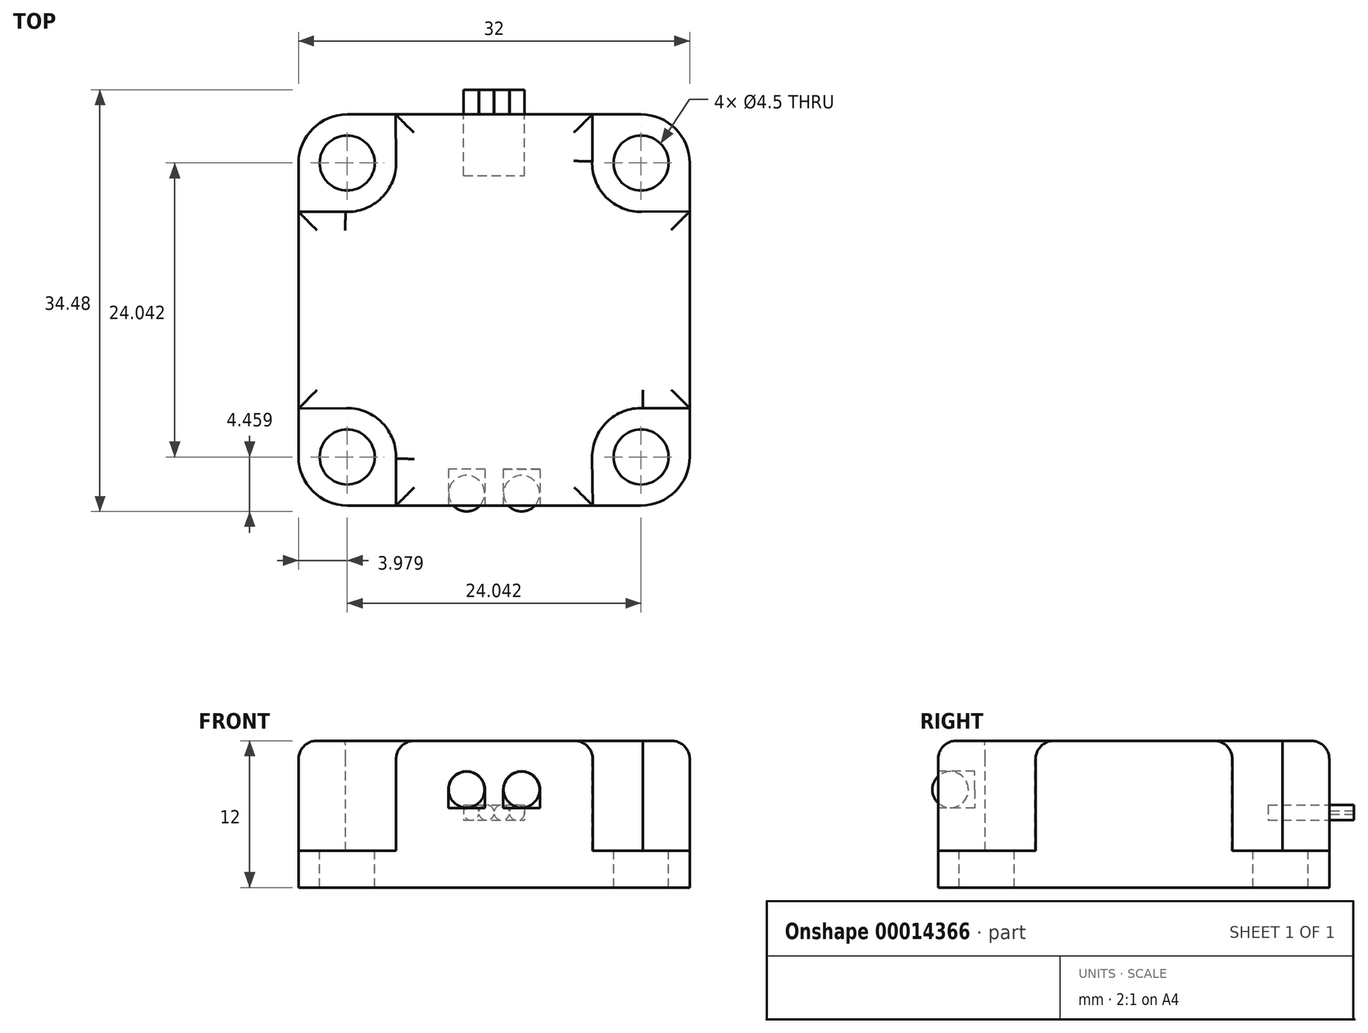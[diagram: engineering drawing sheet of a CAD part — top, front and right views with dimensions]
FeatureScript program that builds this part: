
annotation { "Feature Type Name" : "Feature", "Feature Type Description" : "" }
export const myFeature = defineFeature(function(context is Context, id is Id, definition is map)
    precondition{}
    {
        {
            var Q0;
            Q0=qCreatedBy(makeId("Top.planeOp"),FACE);
            var sketch = newSketch(context, id + "F0", { "sketchPlane" : qUnion([Q0])});
            skLineSegment(sketch, "E0.rect.bottom", {"start": v(16, 16) * mm, "end": v(-16, 16) * mm});
            skLineSegment(sketch, "E0.rect.top", {"start": v(16, -16) * mm, "end": v(-16, -16) * mm});
            skLineSegment(sketch, "E0.rect.left", {"start": v(16, 16) * mm, "end": v(16, -16) * mm});
            skLineSegment(sketch, "E0.rect.right", {"start": v(-16, 16) * mm, "end": v(-16, -16) * mm});
            skPoint(sketch, "E0.rect.middle", {"position": v(0, 0) * mm});
            skSolve(sketch);
        }
        {
            var Q0;
            Q0=qSketchRegion(id+"F0",true);
            extrude(context, id + "F1", {"entities" : qUnion([Q0]), "depth" : 12 * mm});
        }
        {
            var Q0;
            Q0=makeQuery(id+"F1.opExtrude","CAP_FACE",FACE,{"disambiguationData":[OSD([sQuery(id+"F0.wireOp",EDGE,"E0.rect.bottom"),sQuery(id+"F0.wireOp",EDGE,"E0.rect.top"),sQuery(id+"F0.wireOp",EDGE,"E0.rect.left"),sQuery(id+"F0.wireOp",EDGE,"E0.rect.right")])],"isStart":false});
            var sketch = newSketch(context, id + "F2", { "sketchPlane" : qUnion([Q0])});
            skCircle(sketch, "E1", {"center": v(0, 0) * mm, "radius": 17 * mm, "construction": true});
            skLineSegment(sketch, "E2", {"start": v(-16, 16) * mm, "end": v(0, 0) * mm, "construction": true});
            skArc(sketch, "E3", {"start": v(-12.16, 8.02) * mm, "mid": v(-9.22, 9.16) * mm, "end": v(-8.02, 12.07) * mm});
            skLineSegment(sketch, "E4", {"start": v(-8.02, 12.07) * mm, "end": v(-8.07, 16) * mm});
            skLineSegment(sketch, "E5", {"start": v(-8.07, 16) * mm, "end": v(-16, 16) * mm});
            skLineSegment(sketch, "E6", {"start": v(-12.16, 8.02) * mm, "end": v(-16, 8.02) * mm});
            skLineSegment(sketch, "E7", {"start": v(-16, 8.02) * mm, "end": v(-16, 16) * mm});
            skLineSegment(sketch, "E8.1.0", {"start": v(-8.02, -16) * mm, "end": v(-16, -16) * mm});
            skLineSegment(sketch, "E8.1.1", {"start": v(-8.02, -12.16) * mm, "end": v(-8.02, -16) * mm});
            skArc(sketch, "E8.1.2", {"start": v(-8.02, -12.16) * mm, "mid": v(-9.16, -9.22) * mm, "end": v(-12.07, -8.02) * mm});
            skLineSegment(sketch, "E8.1.3", {"start": v(-16, -8.07) * mm, "end": v(-16, -16) * mm});
            skLineSegment(sketch, "E8.1.4", {"start": v(-12.07, -8.02) * mm, "end": v(-16, -8.07) * mm});
            skLineSegment(sketch, "E8.2.0", {"start": v(16, -8.02) * mm, "end": v(16, -16) * mm});
            skLineSegment(sketch, "E8.2.1", {"start": v(12.16, -8.02) * mm, "end": v(16, -8.02) * mm});
            skArc(sketch, "E8.2.2", {"start": v(12.16, -8.02) * mm, "mid": v(9.22, -9.16) * mm, "end": v(8.02, -12.07) * mm});
            skLineSegment(sketch, "E8.2.3", {"start": v(8.07, -16) * mm, "end": v(16, -16) * mm});
            skLineSegment(sketch, "E8.2.4", {"start": v(8.02, -12.07) * mm, "end": v(8.07, -16) * mm});
            skLineSegment(sketch, "E8.3.0", {"start": v(8.02, 16) * mm, "end": v(16, 16) * mm});
            skLineSegment(sketch, "E8.3.1", {"start": v(8.02, 12.16) * mm, "end": v(8.02, 16) * mm});
            skArc(sketch, "E8.3.2", {"start": v(8.02, 12.16) * mm, "mid": v(9.16, 9.22) * mm, "end": v(12.07, 8.02) * mm});
            skLineSegment(sketch, "E8.3.3", {"start": v(16, 8.07) * mm, "end": v(16, 16) * mm});
            skLineSegment(sketch, "E8.3.4", {"start": v(12.07, 8.02) * mm, "end": v(16, 8.07) * mm});
            skSolve(sketch);
        }
        {
            var Q0;
            Q0=qSketchRegion(id+"F2",true);
            extrude(context, id + "F3", {"entities" : qUnion([Q0]), "operationType" : NewBodyOperationType.REMOVE, "oppositeDirection" : true, "depth" : 9 * mm});
        }
        {
            var Q0;
            Q0=makeQuery(id+"F1.opExtrude","SWEPT_EDGE",EDGE,{"disambiguationData":[OSD([sQuery(id+"F0.wireOp",EDGE,"E0.rect.bottom"),sQuery(id+"F0.wireOp",EDGE,"E0.rect.right")])]});
            var Q1;
            Q1=makeQuery(id+"F1.opExtrude","SWEPT_EDGE",EDGE,{"disambiguationData":[OSD([sQuery(id+"F0.wireOp",EDGE,"E0.rect.bottom"),sQuery(id+"F0.wireOp",EDGE,"E0.rect.left")])]});
            var Q2;
            Q2=makeQuery(id+"F1.opExtrude","SWEPT_EDGE",EDGE,{"disambiguationData":[OSD([sQuery(id+"F0.wireOp",EDGE,"E0.rect.top"),sQuery(id+"F0.wireOp",EDGE,"E0.rect.left")])]});
            var Q3;
            Q3=makeQuery(id+"F1.opExtrude","SWEPT_EDGE",EDGE,{"disambiguationData":[OSD([sQuery(id+"F0.wireOp",EDGE,"E0.rect.top"),sQuery(id+"F0.wireOp",EDGE,"E0.rect.right")])]});
            fillet(context, id + "F4", {"entities" : qUnion([Q0, Q1, Q2, Q3]), "radius" : 4 * mm, "tangentPropagation" : true, "allowEdgeOverflow" : false});
        }
        {
            var Q0;
            Q0=makeQuery(id+"F1.opExtrude","CAP_FACE",FACE,{"disambiguationData":[OSD([sQuery(id+"F0.wireOp",EDGE,"E0.rect.bottom"),sQuery(id+"F0.wireOp",EDGE,"E0.rect.top"),sQuery(id+"F0.wireOp",EDGE,"E0.rect.left"),sQuery(id+"F0.wireOp",EDGE,"E0.rect.right")])],"isStart":false});
            var Q1;
            Q1=makeQuery(id+"F3.boolean.opBoolean","COPY",EDGE,{"derivedFrom":makeQuery(id+"F3.opExtrude","SWEPT_EDGE",EDGE,{"disambiguationData":[OSD([sQuery(id+"F0.wireOp",EDGE,"E0.rect.top"),sQuery(id+"F2.wireOp",EDGE,"E8.2.3"),sQuery(id+"F2.wireOp",EDGE,"E8.2.4")])]})});
            var Q2;
            Q2=makeQuery(id+"F3.boolean.opBoolean","COPY",EDGE,{"derivedFrom":makeQuery(id+"F3.opExtrude","SWEPT_EDGE",EDGE,{"disambiguationData":[OSD([sQuery(id+"F0.wireOp",EDGE,"E0.rect.left"),sQuery(id+"F2.wireOp",EDGE,"E8.2.0"),sQuery(id+"F2.wireOp",EDGE,"E8.2.1")])]})});
            var Q3;
            Q3=makeQuery(id+"F3.boolean.opBoolean","COPY",EDGE,{"derivedFrom":makeQuery(id+"F3.opExtrude","SWEPT_EDGE",EDGE,{"disambiguationData":[OSD([sQuery(id+"F0.wireOp",EDGE,"E0.rect.left"),sQuery(id+"F2.wireOp",EDGE,"E8.3.3"),sQuery(id+"F2.wireOp",EDGE,"E8.3.4")])]})});
            var Q4;
            Q4=makeQuery(id+"F3.boolean.opBoolean","COPY",EDGE,{"derivedFrom":makeQuery(id+"F3.opExtrude","SWEPT_EDGE",EDGE,{"disambiguationData":[OSD([sQuery(id+"F0.wireOp",EDGE,"E0.rect.top"),sQuery(id+"F2.wireOp",EDGE,"E8.1.0"),sQuery(id+"F2.wireOp",EDGE,"E8.1.1")])]})});
            var Q5;
            Q5=makeQuery(id+"F3.boolean.opBoolean","COPY",EDGE,{"derivedFrom":makeQuery(id+"F3.opExtrude","SWEPT_EDGE",EDGE,{"disambiguationData":[OSD([sQuery(id+"F0.wireOp",EDGE,"E0.rect.right"),sQuery(id+"F2.wireOp",EDGE,"E8.1.3"),sQuery(id+"F2.wireOp",EDGE,"E8.1.4")])]})});
            var Q6;
            Q6=makeQuery(id+"F3.boolean.opBoolean","COPY",EDGE,{"derivedFrom":makeQuery(id+"F3.opExtrude","SWEPT_EDGE",EDGE,{"disambiguationData":[OSD([sQuery(id+"F0.wireOp",EDGE,"E0.rect.bottom"),sQuery(id+"F2.wireOp",EDGE,"E8.3.0"),sQuery(id+"F2.wireOp",EDGE,"E8.3.1")])]})});
            var Q7;
            Q7=makeQuery(id+"F3.boolean.opBoolean","COPY",EDGE,{"derivedFrom":makeQuery(id+"F3.opExtrude","SWEPT_EDGE",EDGE,{"disambiguationData":[OSD([sQuery(id+"F0.wireOp",EDGE,"E0.rect.bottom"),sQuery(id+"F2.wireOp",EDGE,"E4"),sQuery(id+"F2.wireOp",EDGE,"E5")])]})});
            var Q8;
            Q8=makeQuery(id+"F3.boolean.opBoolean","COPY",EDGE,{"derivedFrom":makeQuery(id+"F3.opExtrude","SWEPT_EDGE",EDGE,{"disambiguationData":[OSD([sQuery(id+"F0.wireOp",EDGE,"E0.rect.right"),sQuery(id+"F2.wireOp",EDGE,"E6"),sQuery(id+"F2.wireOp",EDGE,"E7")])]})});
            fillet(context, id + "F5", {"entities" : qUnion([Q0, Q1, Q2, Q3, Q4, Q5, Q6, Q7, Q8]), "radius" : 1.5 * mm, "tangentPropagation" : true, "allowEdgeOverflow" : false});
        }
        {
            var Q0;
            Q0=makeQuery(id+"F1.opExtrude","SWEPT_FACE",FACE,{"disambiguationData":[OSD([sQuery(id+"F0.wireOp",EDGE,"E0.rect.top")])]});
            var sketch = newSketch(context, id + "F6", { "sketchPlane" : qUnion([Q0])});
            skLineSegment(sketch, "E9", {"start": v(0, 0) * mm, "end": v(0, 16) * mm, "construction": true});
            skLineSegment(sketch, "E10", {"start": v(0, 8) * mm, "end": v(2.25, 8) * mm, "construction": true});
            skArc(sketch, "E11", {"start": v(3.75, 8) * mm, "mid": v(2.25, 9.5) * mm, "end": v(0.75, 8) * mm});
            skLineSegment(sketch, "E12.top", {"start": v(0.75, 6.5) * mm, "end": v(3.75, 6.5) * mm});
            skLineSegment(sketch, "E12.left", {"start": v(0.75, 8) * mm, "end": v(0.75, 6.5) * mm});
            skLineSegment(sketch, "E12.right", {"start": v(3.75, 8) * mm, "end": v(3.75, 6.5) * mm});
            skLineSegment(sketch, "E13.0.MirrorCS", {"start": v(-0.75, 6.5) * mm, "end": v(-3.75, 6.5) * mm});
            skLineSegment(sketch, "E13.1.MirrorCS", {"start": v(-0.75, 8) * mm, "end": v(-0.75, 6.5) * mm});
            skLineSegment(sketch, "E13.2.MirrorCS", {"start": v(-3.75, 8) * mm, "end": v(-3.75, 6.5) * mm});
            skArc(sketch, "E13.3.MirrorCS", {"start": v(-3.75, 8) * mm, "mid": v(-2.25, 9.5) * mm, "end": v(-0.75, 8) * mm});
            skSolve(sketch);
        }
        {
            var Q0;
            Q0=qSketchRegion(id+"F6",true);
            extrude(context, id + "F7", {"entities" : qUnion([Q0]), "operationType" : NewBodyOperationType.REMOVE, "oppositeDirection" : true, "depth" : 3 * mm});
        }
        {
            var Q0;
            Q0=makeQuery(id+"F1.opExtrude","SWEPT_FACE",FACE,{"disambiguationData":[OSD([sQuery(id+"F0.wireOp",EDGE,"E0.rect.bottom")])]});
            var sketch = newSketch(context, id + "F8", { "sketchPlane" : qUnion([Q0])});
            skLineSegment(sketch, "E14.rect.bottom", {"start": v(2.5, 6.75) * mm, "end": v(-2.5, 6.75) * mm});
            skLineSegment(sketch, "E14.rect.top", {"start": v(2.5, 5.5) * mm, "end": v(-2.5, 5.5) * mm});
            skLineSegment(sketch, "E14.rect.left", {"start": v(2.5, 6.75) * mm, "end": v(2.5, 5.5) * mm});
            skLineSegment(sketch, "E14.rect.right", {"start": v(-2.5, 6.75) * mm, "end": v(-2.5, 5.5) * mm});
            skPoint(sketch, "E14.rect.middle", {"position": v(0, 6.12) * mm});
            skSolve(sketch);
        }
        {
            var Q0;
            Q0=qSketchRegion(id+"F8",true);
            extrude(context, id + "F9", {"entities" : qUnion([Q0]), "operationType" : NewBodyOperationType.REMOVE, "oppositeDirection" : true, "depth" : 5 * mm});
        }
        {
            var Q0;
            Q0=makeQuery(id+"F1.opExtrude","SWEPT_FACE",FACE,{"disambiguationData":[OSD([sQuery(id+"F0.wireOp",EDGE,"E0.rect.bottom")])]});
            var sketch = newSketch(context, id + "F10", { "sketchPlane" : qUnion([Q0])});
            skArc(sketch, "E15", {"start": v(1.27, 5.97) * mm, "mid": v(2.5, 6.14) * mm, "end": v(1.26, 6.25) * mm});
            skLineSegment(sketch, "E16", {"start": v(2.5, 6.12) * mm, "end": v(-2.5, 6.12) * mm, "construction": true});
            skArc(sketch, "E17.1.0.0", {"start": v(0.02, 5.97) * mm, "mid": v(0.63, 5.5) * mm, "end": v(1.23, 5.97) * mm});
            skArc(sketch, "E17.2.0.0", {"start": v(-1.23, 5.97) * mm, "mid": v(-0.62, 5.5) * mm, "end": v(-0.02, 5.97) * mm});
            skArc(sketch, "E17.3.0.0", {"start": v(-1.26, 6.25) * mm, "mid": v(-2.5, 6.14) * mm, "end": v(-1.27, 5.97) * mm});
            skLineSegment(sketch, "E17.direction1", {"start": v(1.88, 6.12) * mm, "end": v(0.63, 6.12) * mm, "construction": true});
            skLineSegment(sketch, "E18.rect.bottom", {"start": v(-1.26, 6.25) * mm, "end": v(-1.24, 6.25) * mm});
            skLineSegment(sketch, "E18.rect.top", {"start": v(-1.27, 5.97) * mm, "end": v(-1.23, 5.97) * mm});
            skPoint(sketch, "E18.rect.middle", {"position": v(0, 6.13) * mm});
            skLineSegment(sketch, "E19.trimOffspring", {"start": v(-0.01, 6.25) * mm, "end": v(0.01, 6.25) * mm});
            skArc(sketch, "E20.trimOffspring", {"start": v(-0.01, 6.25) * mm, "mid": v(-0.62, 6.75) * mm, "end": v(-1.24, 6.25) * mm});
            skLineSegment(sketch, "E21.trimOffspring", {"start": v(1.24, 6.25) * mm, "end": v(1.26, 6.25) * mm});
            skLineSegment(sketch, "E22.trimOffspring", {"start": v(1.23, 5.97) * mm, "end": v(1.27, 5.97) * mm});
            skArc(sketch, "E23.trimOffspring", {"start": v(1.24, 6.25) * mm, "mid": v(0.63, 6.75) * mm, "end": v(0.01, 6.25) * mm});
            skLineSegment(sketch, "E24", {"start": v(-0.02, 5.97) * mm, "end": v(0.02, 5.97) * mm});
            skSolve(sketch);
        }
        {
            var Q0;
            Q0=qSketchRegion(id+"F10",true);
            extrude(context, id + "F11", {"entities" : qUnion([Q0]), "operationType" : NewBodyOperationType.ADD, "depth" : 2 * mm});
        }
        {
            var Q0;
            Q0=makeQuery(id+"F1.opExtrude","SWEPT_FACE",FACE,{"disambiguationData":[OSD([sQuery(id+"F0.wireOp",EDGE,"E0.rect.top")])]});
            cPlane(context, id + "F12", {"entities" : qUnion([Q0]), "cplaneType" : CPlaneType.OFFSET, "offset" : 1 * mm, "oppositeDirection" : true, "width" : 152.4 * mm, "height" : 152.4 * mm});
        }
        {
            var Q0;
            Q0=qCreatedBy(id+"F12.planeOp",FACE);
            var sketch = newSketch(context, id + "F13", { "sketchPlane" : qUnion([Q0])});
            skArc(sketch, "E25", {"start": v(0.77, 8) * mm, "mid": v(2.25, 6.52) * mm, "end": v(3.72, 8) * mm});
            skLineSegment(sketch, "E26", {"start": v(2.25, 8) * mm, "end": v(-2.18, 8) * mm, "construction": true});
            skLineSegment(sketch, "E27", {"start": v(0, 8) * mm, "end": v(0, 9.48) * mm, "construction": true});
            skArc(sketch, "E28.0.MirrorC", {"start": v(-0.77, 8) * mm, "mid": v(-2.25, 6.52) * mm, "end": v(-3.72, 8) * mm});
            skLineSegment(sketch, "E29", {"start": v(3.72, 8) * mm, "end": v(0.77, 8) * mm});
            skLineSegment(sketch, "E30.trimOffspring", {"start": v(-0.77, 8) * mm, "end": v(-3.72, 8) * mm});
            skSolve(sketch);
        }
        {
            var Q0;
            Q0=qSketchRegion(id+"F13",true);
            var Q1;
            Q1=sQuery(id+"F13.wireOp",EDGE,"E26");
            revolve(context, id + "F14", {"operationType" : NewBodyOperationType.ADD, "entities" : qUnion([Q0]), "axis" : qUnion([Q1]), "revolveType" : RevolveType.FULL});
        }
        {
            var Q0;
            Q0=makeQuery(id+"F3.boolean.opBoolean","COPY",FACE,{"derivedFrom":makeQuery(id+"F3.opExtrude","CAP_FACE",FACE,{"disambiguationData":[OSD([sQuery(id+"F2.wireOp",EDGE,"E8.3.0"),sQuery(id+"F2.wireOp",EDGE,"E8.3.1"),sQuery(id+"F2.wireOp",EDGE,"E8.3.2"),sQuery(id+"F2.wireOp",EDGE,"E8.3.3"),sQuery(id+"F2.wireOp",EDGE,"E8.3.4")])],"isStart":false})});
            var sketch = newSketch(context, id + "F15", { "sketchPlane" : qUnion([Q0])});
            skCircle(sketch, "E31", {"center": v(0, 0) * mm, "radius": 17 * mm, "construction": true});
            skLineSegment(sketch, "E32", {"start": v(0, 0) * mm, "end": v(14.83, 14.83) * mm, "construction": true});
            skCircle(sketch, "E33", {"center": v(12.02, 12.02) * mm, "radius": 2.25 * mm});
            skCircle(sketch, "E34.1.0", {"center": v(-12.02, 12.02) * mm, "radius": 2.25 * mm});
            skCircle(sketch, "E34.2.0", {"center": v(-12.02, -12.02) * mm, "radius": 2.25 * mm});
            skCircle(sketch, "E34.3.0", {"center": v(12.02, -12.02) * mm, "radius": 2.25 * mm});
            skSolve(sketch);
        }
        {
            var Q0;
            Q0=qSketchRegion(id+"F15",true);
            extrude(context, id + "F16", {"entities" : qUnion([Q0]), "operationType" : NewBodyOperationType.REMOVE, "endBound" : BoundingType.THROUGH_ALL, "oppositeDirection" : true, "depth" : 25.4 * mm});
        }
    });
